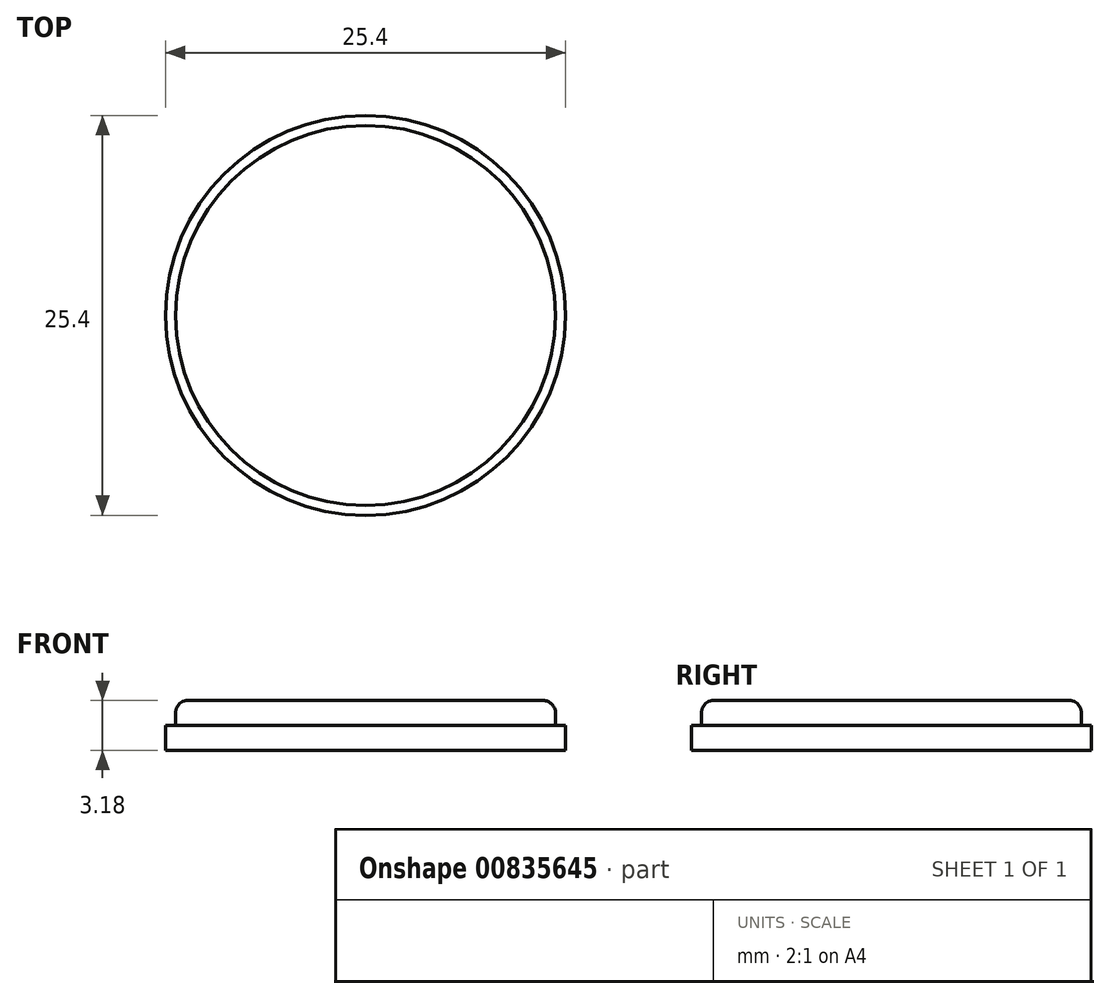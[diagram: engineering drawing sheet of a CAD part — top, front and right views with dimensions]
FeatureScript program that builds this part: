
annotation { "Feature Type Name" : "Feature", "Feature Type Description" : "" }
export const myFeature = defineFeature(function(context is Context, id is Id, definition is map)
    precondition{}
    {
        {
            var Q0;
            Q0=qCreatedBy(makeId("Top.planeOp"),FACE);
            var sketch = newSketch(context, id + "F0", { "sketchPlane" : qUnion([Q0])});
            skCircle(sketch, "E0", {"center": v(0, 0) * mm, "radius": 12.7 * mm});
            skSolve(sketch);
        }
        {
            var Q0;
            Q0 = qSketchRegion(id + "F0", true);
            extrude(context, id + "F1", {"entities" : qUnion([Q0]), "depth" : 1.59 * mm, "offsetDistance" : 25.4 * mm});
        }
        {
            var Q0;
            Q0=makeQuery(id+"F1.opExtrude","CAP_FACE",FACE,{"disambiguationData":[OSD([sQuery(id+"F0.wireOp",EDGE,"E0")])],"isStart":false});
            var sketch = newSketch(context, id + "F2", { "sketchPlane" : qUnion([Q0])});
            skCircle(sketch, "E1", {"center": v(0, 0) * mm, "radius": 12.07 * mm});
            skSolve(sketch);
        }
        {
            var Q0;
            Q0=makeQuery(id+"F2.imprint","IMPRINT",FACE,{"disambiguationData":[TD([[makeQuery(id+"F2.imprint","IMPRINT",EDGE,{"derivedFrom":sQuery(id+"F2.wireOp",EDGE,"E1")}),1.0]])]});
            extrude(context, id + "F3", {"entities" : qUnion([Q0]), "operationType" : NewBodyOperationType.ADD, "depth" : 1.59 * mm, "offsetDistance" : 25.4 * mm});
        }
        {
            var Q0;
            Q0=makeQuery(id+"F3.opExtrude","CAP_EDGE",EDGE,{"disambiguationData":[OSD([sQuery(id+"F2.wireOp",EDGE,"E1")])],"isStart":false});
            fillet(context, id + "F4", {"entities" : qUnion([Q0]), "radius" : 0.8 * mm, "tangentPropagation" : true, "allowEdgeOverflow" : false});
        }
    });
